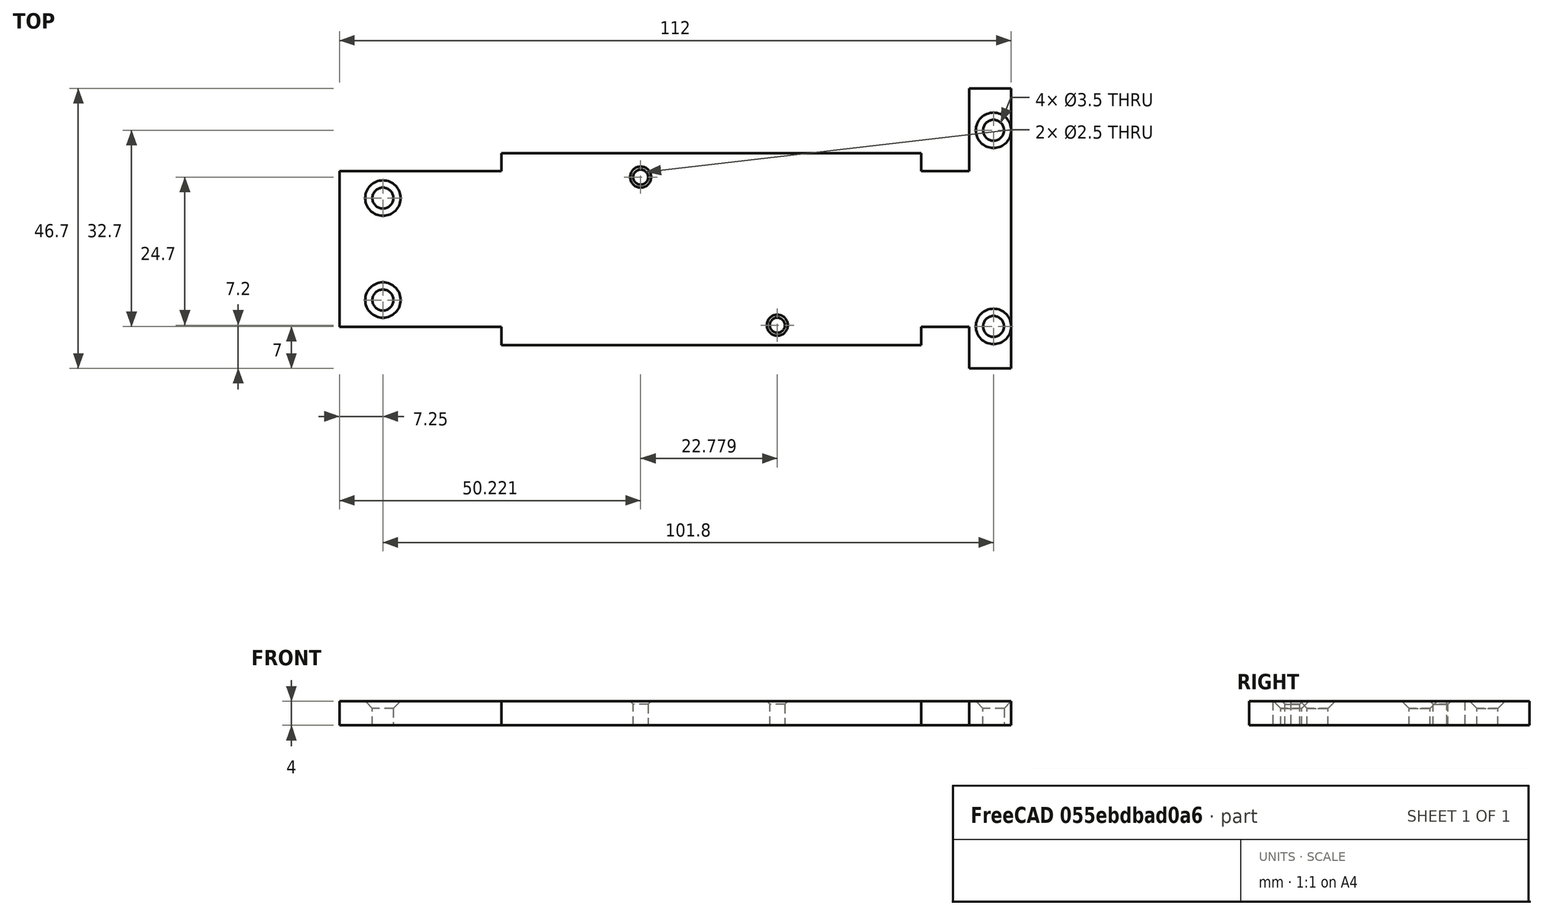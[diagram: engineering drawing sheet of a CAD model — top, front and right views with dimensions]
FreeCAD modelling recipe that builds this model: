
FCSTD DOCUMENT  (FreeCAD 0.18R16146 (Git))
Label: topDeckBack
License: All rights reserved
LicenseURL: http://en.wikipedia.org/wiki/All_rights_reserved
objects: PartDesign::Chamfer×2, Mesh::Feature×1, Sketcher::SketchObject×1, PartDesign::Pad×1, PartDesign::Body×1
note: 6 computed .brp shape members not serialized (recipe doc carries the construction recipe); baked Part::Feature solids carry a one-line shape summary decoded from their .brp

FEATURE [Mesh::Feature] Top_Deck_Rear
  Placement = pos=(0,0,0) rot=(1,0,0;3.14159rad)
FEATURE [Sketcher::SketchObject] Sketch
  MapMode = 5
  Support = -> [XY_Plane]
  sketch-geometry (24):
    g0: LineSegment StartX=-61.5 StartY=13 StartZ=0 EndX=-34.5 EndY=13 EndZ=0
    g1: LineSegment StartX=-61.5 StartY=-13 StartZ=0 EndX=-61.5 EndY=13 EndZ=0
    g2: LineSegment StartX=43.5 StartY=26.8 StartZ=0 EndX=50.5 EndY=26.8 EndZ=0
    g3: LineSegment StartX=50.5 StartY=26.8 StartZ=0 EndX=50.5 EndY=-19.9 EndZ=0
    g4: LineSegment StartX=50.5 StartY=-19.9 StartZ=0 EndX=43.5 EndY=-19.9 EndZ=0
    g5: LineSegment StartX=43.5 StartY=-19.9 StartZ=0 EndX=43.5 EndY=-13 EndZ=0
    g6: LineSegment StartX=43.5 StartY=13 StartZ=0 EndX=43.5 EndY=26.8 EndZ=0
    g7: LineSegment StartX=43.5 StartY=-13 StartZ=0 EndX=35.5 EndY=-13 EndZ=0
    g8: Circle CenterX=47.55 CenterY=19.8 CenterZ=0 NormalX=0 NormalY=0 NormalZ=1 AngleXU=0 Radius=1.75
    g9: Circle CenterX=47.55 CenterY=-12.9 CenterZ=0 NormalX=0 NormalY=0 NormalZ=1 AngleXU=0 Radius=1.75
    g10: LineSegment [constr] StartX=47.55 StartY=19.8 StartZ=0 EndX=47.55 EndY=-12.9 EndZ=0
    g11: Circle CenterX=-54.25 CenterY=8.5 CenterZ=0 NormalX=0 NormalY=0 NormalZ=1 AngleXU=0 Radius=1.75
    g12: LineSegment [constr] StartX=-54.25 StartY=8.5 StartZ=0 EndX=-54.25 EndY=-8.5 EndZ=0
    g13: Circle CenterX=-54.25 CenterY=-8.5 CenterZ=0 NormalX=0 NormalY=0 NormalZ=1 AngleXU=0 Radius=1.75
    g14: LineSegment StartX=-34.5 StartY=16 StartZ=0 EndX=35.5 EndY=16 EndZ=0
    g15: LineSegment StartX=35.5 StartY=16 StartZ=0 EndX=35.5 EndY=13 EndZ=0
    g16: LineSegment StartX=35.5 StartY=-16 StartZ=0 EndX=-34.5 EndY=-16 EndZ=0
    g17: LineSegment StartX=-34.5 StartY=-16 StartZ=0 EndX=-34.5 EndY=-13 EndZ=0
    g18: LineSegment StartX=35.5 StartY=13 StartZ=0 EndX=43.5 EndY=13 EndZ=0
    g19: LineSegment StartX=-34.5 StartY=-13 StartZ=0 EndX=-61.5 EndY=-13 EndZ=0
    g20: LineSegment StartX=35.5 StartY=-13 StartZ=0 EndX=35.5 EndY=-16 EndZ=0
    g21: LineSegment StartX=-34.5 StartY=13 StartZ=0 EndX=-34.5 EndY=16 EndZ=0
    g22: Circle CenterX=-11.2787 CenterY=12 CenterZ=0 NormalX=0 NormalY=0 NormalZ=1 AngleXU=0 Radius=1.25
    g23: Circle CenterX=11.5 CenterY=-12.7 CenterZ=0 NormalX=0 NormalY=0 NormalZ=1 AngleXU=0 Radius=1.25
  constraints (65):
    c: Coincident(g19,g1)
    c: Coincident(g1,g0)
    c: Horizontal(g0)
    c: Vertical(g1)
    c: Distance(g1) = 26
    c: Distance(g0,g-1) = 13
    c: Coincident(g2,g3)
    c: Coincident(g3,g4)
    c: Coincident(g4,g5)
    c: Coincident(g6,g2)
    c: Horizontal(g2)
    c: Horizontal(g4)
    c: Vertical(g3)
    c: Vertical(g5)
    c: Coincident(g6,g18)
    c: Tangent(g5,g6)
    c: Coincident(g7,g5)
    c: Distance(g2) = 7
    c: DistanceX(g-2,g1) = -61.5
    c: Distance(g0,g3) = 112
    c: Radius(g8) = 1.75
    c: DistanceY(g-1,g8) = 19.8
    c: DistanceX(g-2,g8) = 47.55
    c: Distance(g8,g2) = 7
    c: Equal(g8,g9) = 1.75
    c: DistanceY(g-1,g9) = -12.9
    c: Coincident(g10,g8)
    c: Coincident(g10,g9)
    c: Parallel(g10,g-2)
    c: Distance(g9,g4) = 7
    c: Equal(g8,g11) = 1.75
    c: Equal(g11,g13) = 1.75
    c: Coincident(g12,g11)
    c: Coincident(g12,g13)
    c: Parallel(g12,g-2)
    c: DistanceY(g-1,g13) = -8.5
    c: DistanceY(g-1,g11) = 8.5
    c: DistanceX(g-2,g11) = -54.25
    c: Coincident(g14,g15)
    c: Coincident(g20,g16)
    c: Coincident(g16,g17)
    c: Coincident(g21,g14)
    c: Horizontal(g14)
    c: Horizontal(g16)
    c: Vertical(g15)
    c: Vertical(g17)
    c: Distance(g14) = 70
    c: Distance(g14,g6) = 8
    c: DistanceY(g-1,g14) = 16
    c: Tangent(g0,g18)
    c: Tangent(g7,g19)
    c: Coincident(g15,g18)
    c: Coincident(g20,g7)
    c: Tangent(g15,g20)
    c: Coincident(g17,g19)
    c: Coincident(g21,g0)
    c: Tangent(g17,g21)
    c: DistanceY(g-1,g16) = -16
    c: Parallel(g18,g7)
    c: Distance(g22,g14) = 4
    c: Distance(g23,g16) = 3.3
    c: Distance(g22,g23) = 33.6
    c: Distance(g23,g20) = 24
    c: Radius(g23) = 1.25
    c: Equal(g23,g22)
FEATURE [PartDesign::Pad] Pad
  Length = 4
  Length2 = 100
  Profile = -> Sketch
  Reversed = true
  Type = 0
FEATURE [PartDesign::Chamfer] Chamfer
  Base = -> Pad [Edge53,Edge50,Edge56,Edge59]
  BaseFeature = -> Pad
  Size = 1.2
FEATURE [PartDesign::Chamfer] Chamfer001
  Base = -> Chamfer [Edge49,Edge48]
  BaseFeature = -> Chamfer
  Size = 0.5
FEATURE [PartDesign::Body] Body
  Group = -> [Sketch,Pad,Chamfer,Chamfer001]
  Origin = -> Origin
  Tip = -> Chamfer001
